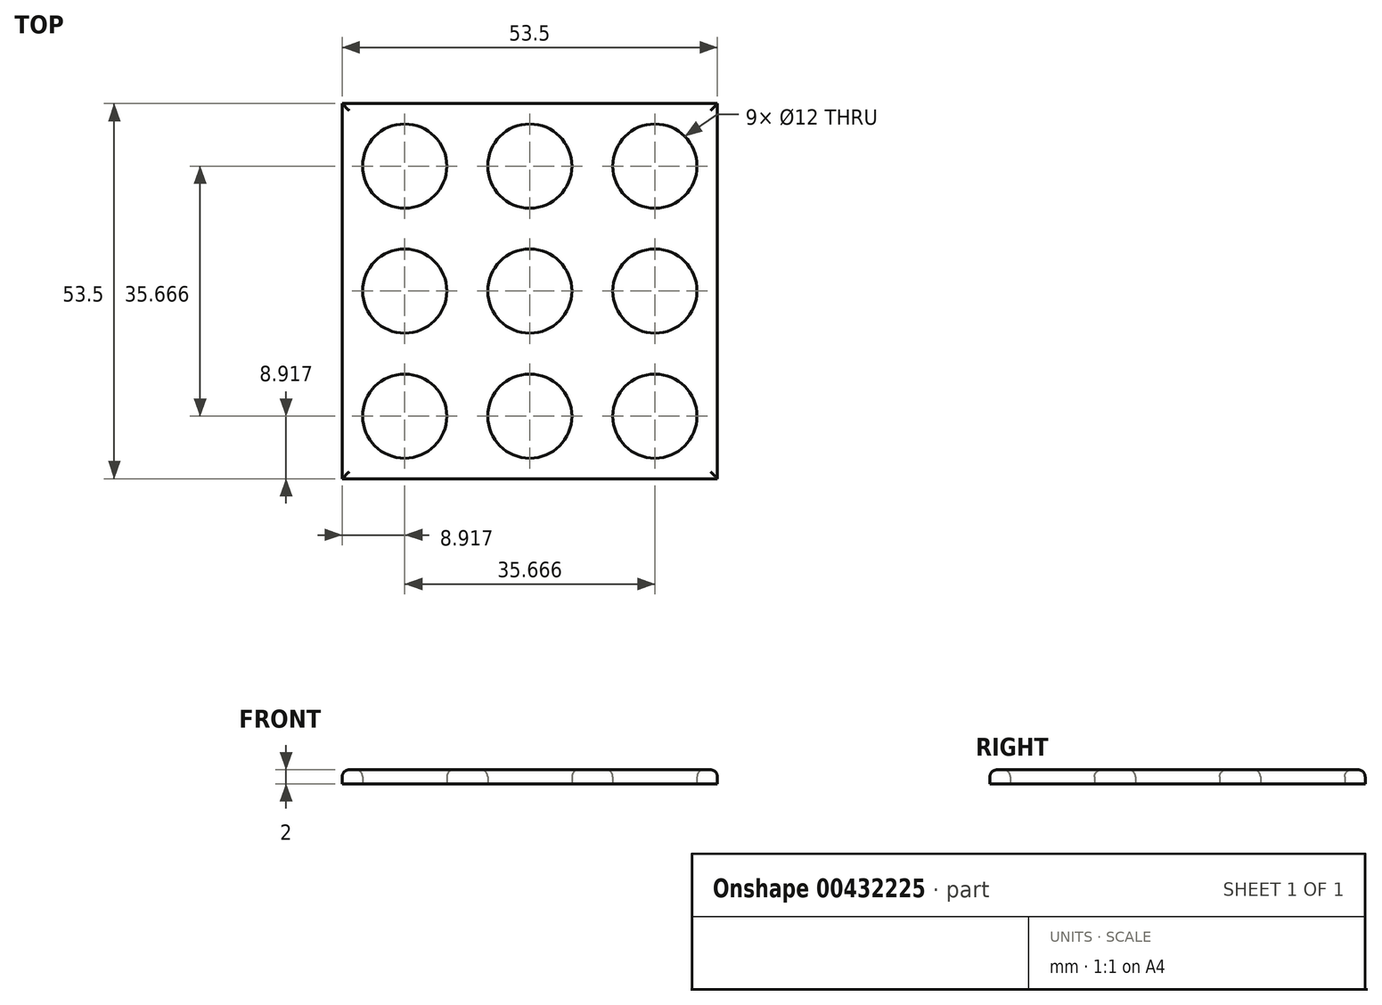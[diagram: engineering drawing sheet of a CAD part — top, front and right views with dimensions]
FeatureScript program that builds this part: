
annotation { "Feature Type Name" : "Feature", "Feature Type Description" : "" }
export const myFeature = defineFeature(function(context is Context, id is Id, definition is map)
    precondition{}
    {
        {
            var Q0;
            Q0=qCreatedBy(makeId("Top.planeOp"),FACE);
            var sketch = newSketch(context, id + "F0", { "sketchPlane" : qUnion([Q0])});
            skLineSegment(sketch, "E0.bottom", {"start": v(26.75, 26.75) * mm, "end": v(-26.75, 26.75) * mm});
            skLineSegment(sketch, "E0.top", {"start": v(26.75, -26.75) * mm, "end": v(-26.75, -26.75) * mm});
            skLineSegment(sketch, "E0.left", {"start": v(26.75, 26.75) * mm, "end": v(26.75, -26.75) * mm});
            skLineSegment(sketch, "E0.right", {"start": v(-26.75, 26.75) * mm, "end": v(-26.75, -26.75) * mm});
            skPoint(sketch, "E0.middle", {"position": v(0, 0) * mm});
            skCircle(sketch, "E1", {"center": v(-17.83, 17.83) * mm, "radius": 6 * mm});
            skCircle(sketch, "E2.0.1.0", {"center": v(-17.83, 0) * mm, "radius": 6 * mm});
            skCircle(sketch, "E2.0.2.0", {"center": v(-17.83, -17.83) * mm, "radius": 6 * mm});
            skCircle(sketch, "E2.1.0.0", {"center": v(0, 17.83) * mm, "radius": 6 * mm});
            skCircle(sketch, "E2.1.1.0", {"center": v(0, 0) * mm, "radius": 6 * mm});
            skCircle(sketch, "E2.1.2.0", {"center": v(0, -17.83) * mm, "radius": 6 * mm});
            skCircle(sketch, "E2.2.0.0", {"center": v(17.83, 17.83) * mm, "radius": 6 * mm});
            skCircle(sketch, "E2.2.1.0", {"center": v(17.83, 0) * mm, "radius": 6 * mm});
            skCircle(sketch, "E2.2.2.0", {"center": v(17.83, -17.83) * mm, "radius": 6 * mm});
            skLineSegment(sketch, "E2.direction1", {"start": v(-17.83, 17.83) * mm, "end": v(0, 17.83) * mm, "construction": true});
            skLineSegment(sketch, "E2.direction2", {"start": v(-17.83, 17.83) * mm, "end": v(-17.83, 0) * mm, "construction": true});
            skSolve(sketch);
        }
        {
            var Q0;
            Q0 = qSketchRegion(id + "F0", true);
            extrude(context, id + "F1", {"entities" : qUnion([Q0]), "depth" : 2 * mm});
        }
        {
            var Q0;
            Q0=makeQuery(id+"F1.opExtrude","CAP_FACE",FACE,{"disambiguationData":[OSD([sQuery(id+"F0.wireOp",EDGE,"E0.bottom"),sQuery(id+"F0.wireOp",EDGE,"E0.top"),sQuery(id+"F0.wireOp",EDGE,"E0.left"),sQuery(id+"F0.wireOp",EDGE,"E0.right"),sQuery(id+"F0.wireOp",EDGE,"E1"),sQuery(id+"F0.wireOp",EDGE,"E2.0.1.0"),sQuery(id+"F0.wireOp",EDGE,"E2.0.2.0"),sQuery(id+"F0.wireOp",EDGE,"E2.1.0.0"),sQuery(id+"F0.wireOp",EDGE,"E2.1.1.0"),sQuery(id+"F0.wireOp",EDGE,"E2.1.2.0"),sQuery(id+"F0.wireOp",EDGE,"E2.2.0.0"),sQuery(id+"F0.wireOp",EDGE,"E2.2.1.0"),sQuery(id+"F0.wireOp",EDGE,"E2.2.2.0")])],"isStart":false});
            fillet(context, id + "F2", {"entities" : qUnion([Q0]), "radius" : 1 * mm, "tangentPropagation" : true, "allowEdgeOverflow" : false});
        }
    });
